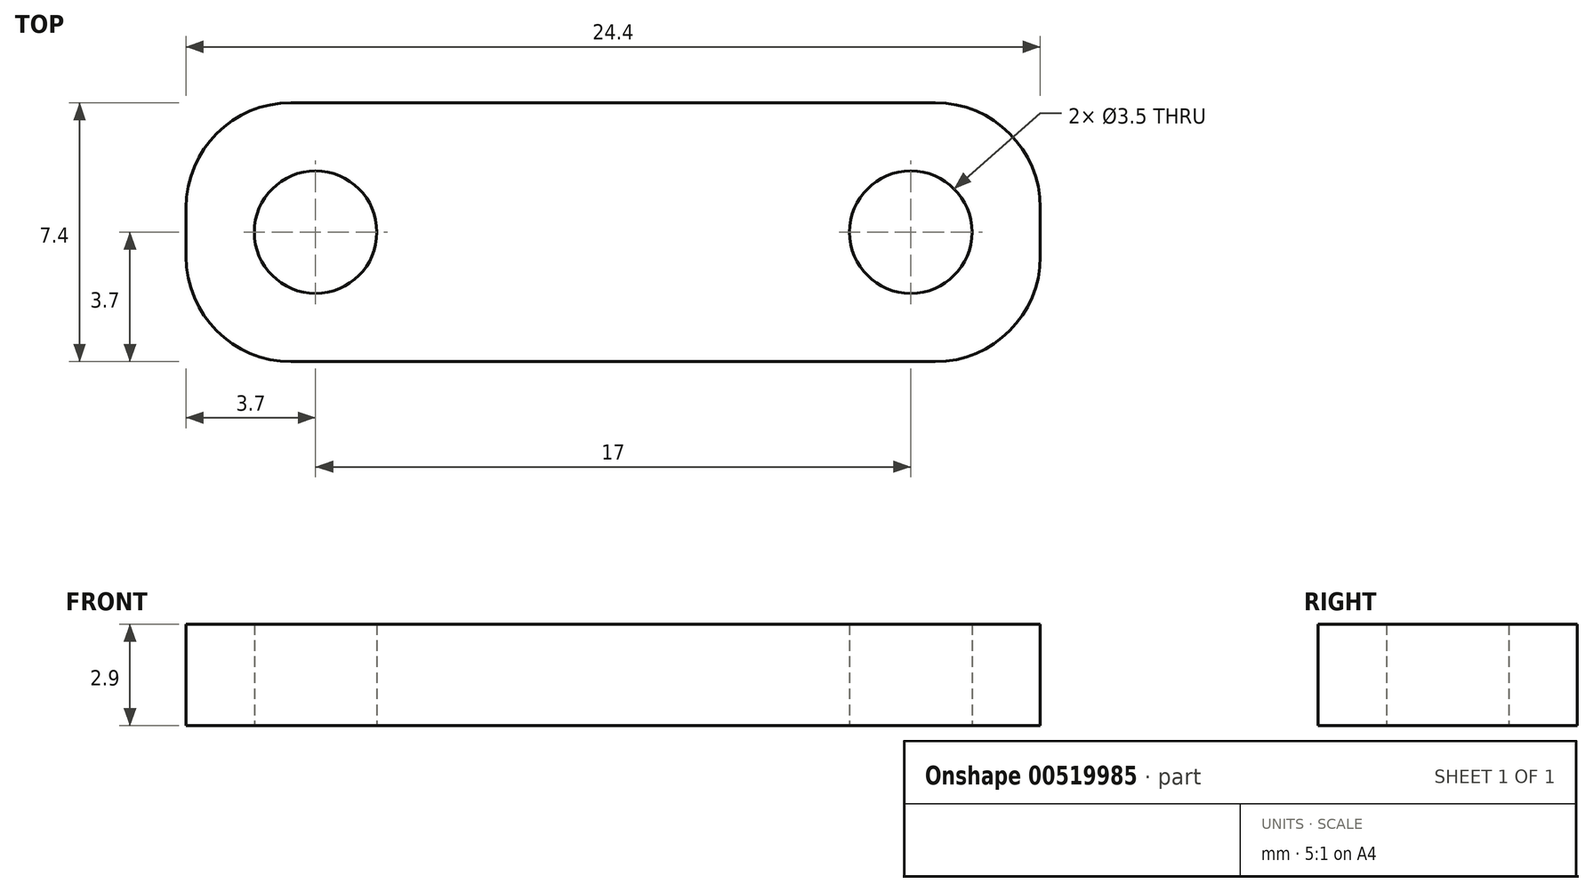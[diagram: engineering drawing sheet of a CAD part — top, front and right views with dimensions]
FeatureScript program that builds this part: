
annotation { "Feature Type Name" : "Feature", "Feature Type Description" : "" }
export const myFeature = defineFeature(function(context is Context, id is Id, definition is map)
    precondition{}
    {
        {
            var Q0;
            Q0=qCreatedBy(makeId("Top.planeOp"),FACE);
            var sketch = newSketch(context, id + "F0", { "sketchPlane" : qUnion([Q0])});
            skLineSegment(sketch, "E0.bottom", {"start": v(0, 0) * mm, "end": v(24.4, 0) * mm});
            skLineSegment(sketch, "E0.top", {"start": v(0, 7.4) * mm, "end": v(24.4, 7.4) * mm});
            skLineSegment(sketch, "E0.left", {"start": v(0, 0) * mm, "end": v(0, 7.4) * mm});
            skLineSegment(sketch, "E0.right", {"start": v(24.4, 0) * mm, "end": v(24.4, 7.4) * mm});
            skCircle(sketch, "E1", {"center": v(3.7, 3.7) * mm, "radius": 1.75 * mm});
            skCircle(sketch, "E2", {"center": v(20.7, 3.7) * mm, "radius": 1.75 * mm});
            skSolve(sketch);
        }
        {
            var Q0;
            Q0 = qSketchRegion(id + "F0", true);
            extrude(context, id + "F1", {"entities" : qUnion([Q0]), "depth" : 2.9 * mm, "offsetDistance" : 25 * mm});
        }
        {
            var Q0;
            Q0=makeQuery(id+"F1.opExtrude","SWEPT_EDGE",EDGE,{"disambiguationData":[OSD([sQuery(id+"F0.wireOp",EDGE,"E0.top"),sQuery(id+"F0.wireOp",EDGE,"E0.left")])]});
            var Q1;
            Q1=makeQuery(id+"F1.opExtrude","SWEPT_EDGE",EDGE,{"disambiguationData":[OSD([sQuery(id+"F0.wireOp",EDGE,"E0.bottom"),sQuery(id+"F0.wireOp",EDGE,"E0.left")])]});
            var Q2;
            Q2=makeQuery(id+"F1.opExtrude","SWEPT_EDGE",EDGE,{"disambiguationData":[OSD([sQuery(id+"F0.wireOp",EDGE,"E0.bottom"),sQuery(id+"F0.wireOp",EDGE,"E0.right")])]});
            var Q3;
            Q3=makeQuery(id+"F1.opExtrude","SWEPT_EDGE",EDGE,{"disambiguationData":[OSD([sQuery(id+"F0.wireOp",EDGE,"E0.top"),sQuery(id+"F0.wireOp",EDGE,"E0.right")])]});
            fillet(context, id + "F2", {"entities" : qUnion([Q0, Q1, Q2, Q3]), "radius" : 3 * mm, "tangentPropagation" : true, "allowEdgeOverflow" : false});
        }
    });
